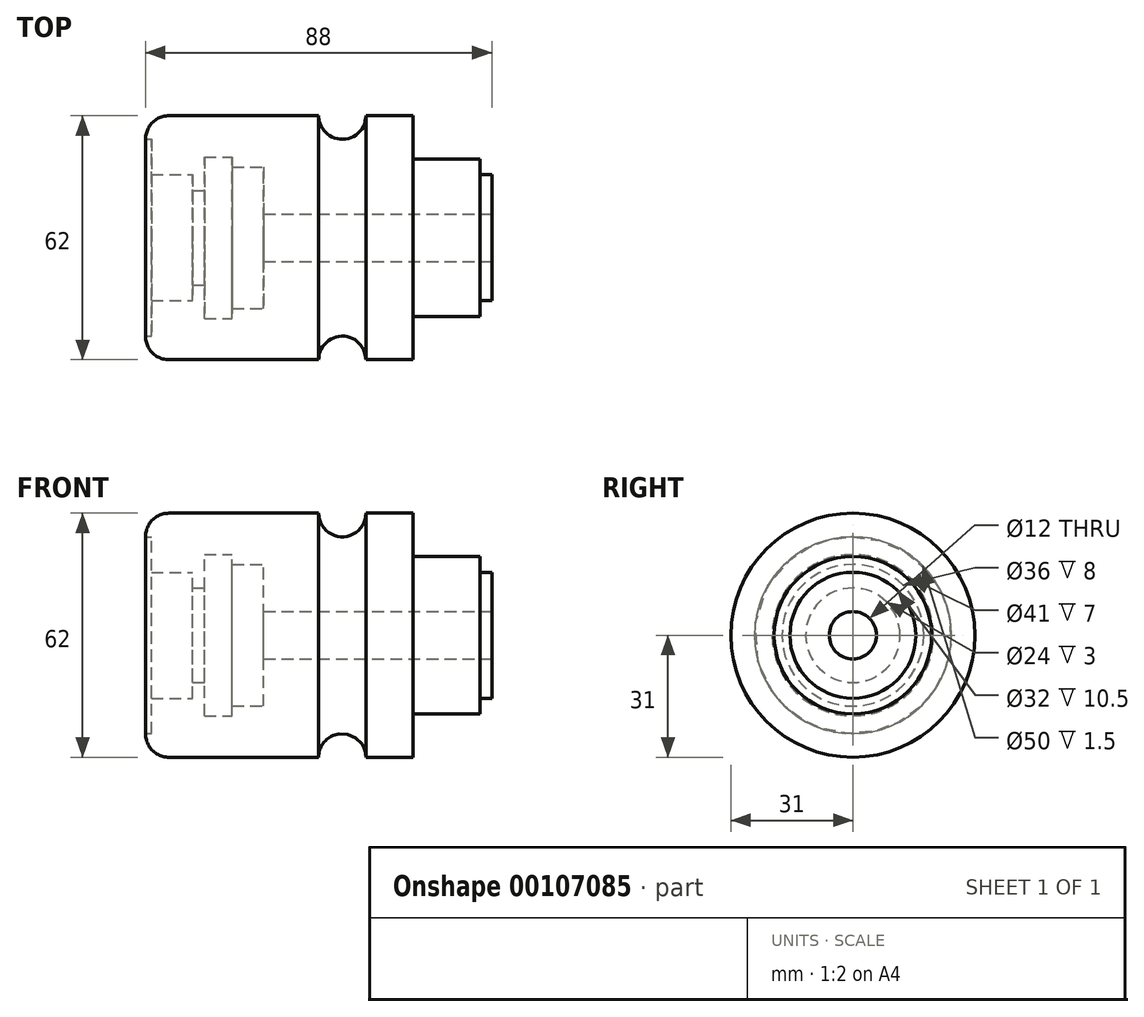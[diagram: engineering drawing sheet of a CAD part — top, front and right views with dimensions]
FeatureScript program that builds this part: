
annotation { "Feature Type Name" : "Feature", "Feature Type Description" : "" }
export const myFeature = defineFeature(function(context is Context, id is Id, definition is map)
    precondition{}
    {
        {
            var Q0;
            Q0=qCreatedBy(makeId("Front.planeOp"),FACE);
            var sketch = newSketch(context, id + "F0", { "sketchPlane" : qUnion([Q0])});
            skLineSegment(sketch, "E0.bottom", {"start": v(0, 0) * mm, "end": v(68, 0) * mm});
            skLineSegment(sketch, "E0.left", {"start": v(0, 0) * mm, "end": v(0, 31) * mm});
            skLineSegment(sketch, "E0.right", {"start": v(68, 0) * mm, "end": v(68, 31) * mm});
            skLineSegment(sketch, "E1.bottom", {"start": v(68, 0) * mm, "end": v(85, 0) * mm});
            skLineSegment(sketch, "E1.top", {"start": v(68, 20) * mm, "end": v(85, 20) * mm});
            skLineSegment(sketch, "E1.left", {"start": v(68, 0) * mm, "end": v(68, 20) * mm});
            skLineSegment(sketch, "E1.right", {"start": v(85, 0) * mm, "end": v(85, 20) * mm});
            skLineSegment(sketch, "E2.bottom", {"start": v(85, 0) * mm, "end": v(88, 0) * mm});
            skLineSegment(sketch, "E2.top", {"start": v(85, 16) * mm, "end": v(88, 16) * mm});
            skLineSegment(sketch, "E2.left", {"start": v(85, 0) * mm, "end": v(85, 16) * mm});
            skLineSegment(sketch, "E2.right", {"start": v(88, 0) * mm, "end": v(88, 16) * mm});
            skLineSegment(sketch, "E3", {"start": v(-75.19, 0) * mm, "end": v(76.5, 0) * mm, "construction": true});
            skArc(sketch, "E4", {"start": v(44, 31) * mm, "mid": v(50, 25) * mm, "end": v(56, 31) * mm});
            skLineSegment(sketch, "E5", {"start": v(0, 31) * mm, "end": v(44, 31) * mm});
            skLineSegment(sketch, "E6", {"start": v(56, 31) * mm, "end": v(68, 31) * mm});
            skSolve(sketch);
        }
        {
            var Q0;
            Q0=makeQuery(id+"F0.imprint","IMPRINT",FACE,{"disambiguationData":[TD([[makeQuery(id+"F0.imprint","IMPRINT",EDGE,{"derivedFrom":sQuery(id+"F0.wireOp",EDGE,"E1.bottom")}),1.0]])]});
            var Q1;
            Q1=makeQuery(id+"F0.imprint","IMPRINT",FACE,{"disambiguationData":[TD([[makeQuery(id+"F0.imprint","IMPRINT",EDGE,{"derivedFrom":sQuery(id+"F0.wireOp",EDGE,"E0.bottom")}),1.0]])]});
            var Q2;
            Q2=makeQuery(id+"F0.imprint","IMPRINT",FACE,{"disambiguationData":[TD([[makeQuery(id+"F0.imprint","IMPRINT",EDGE,{"derivedFrom":sQuery(id+"F0.wireOp",EDGE,"E2.bottom")}),1.0]])]});
            var Q3;
            Q3=sQuery(id+"F0.wireOp",EDGE,"E3");
            revolve(context, id + "F1", {"entities" : qUnion([Q0, Q1, Q2]), "axis" : qUnion([Q3]), "revolveType" : RevolveType.FULL});
        }
        {
            var Q0;
            Q0=qCreatedBy(makeId("Right.planeOp"),FACE);
            var sketch = newSketch(context, id + "F2", { "sketchPlane" : qUnion([Q0])});
            skCircle(sketch, "E7", {"center": v(0, 0) * mm, "radius": 6 * mm});
            skSolve(sketch);
        }
        {
            var Q0;
            Q0 = qSketchRegion(id + "F2", true);
            extrude(context, id + "F3", {"entities" : qUnion([Q0]), "operationType" : NewBodyOperationType.REMOVE, "endBound" : BoundingType.SYMMETRIC, "oppositeDirection" : true, "depth" : 1000 * mm});
        }
        {
            var Q0;
            Q0=qCreatedBy(makeId("Top.planeOp"),FACE);
            var sketch = newSketch(context, id + "F4", { "sketchPlane" : qUnion([Q0])});
            skLineSegment(sketch, "E8.bottom", {"start": v(0, 0) * mm, "end": v(1.5, 0) * mm});
            skLineSegment(sketch, "E8.top", {"start": v(0, 25) * mm, "end": v(1.5, 25) * mm});
            skLineSegment(sketch, "E8.left", {"start": v(0, 0) * mm, "end": v(0, 25) * mm});
            skLineSegment(sketch, "E8.right", {"start": v(1.5, 0) * mm, "end": v(1.5, 25) * mm});
            skLineSegment(sketch, "E9.bottom", {"start": v(0, 0) * mm, "end": v(12, 0) * mm});
            skLineSegment(sketch, "E9.top", {"start": v(0, 16) * mm, "end": v(12, 16) * mm});
            skLineSegment(sketch, "E9.left", {"start": v(0, 0) * mm, "end": v(0, 16) * mm});
            skLineSegment(sketch, "E9.right", {"start": v(12, 0) * mm, "end": v(12, 16) * mm});
            skLineSegment(sketch, "E10.bottom", {"start": v(12, 0) * mm, "end": v(15, 0) * mm});
            skLineSegment(sketch, "E10.top", {"start": v(12, 12) * mm, "end": v(15, 12) * mm});
            skLineSegment(sketch, "E10.left", {"start": v(12, 0) * mm, "end": v(12, 12) * mm});
            skLineSegment(sketch, "E10.right", {"start": v(15, 0) * mm, "end": v(15, 12) * mm});
            skLineSegment(sketch, "E11.left", {"start": v(0, 0) * mm, "end": v(0, 19.39) * mm});
            skLineSegment(sketch, "E12.bottom", {"start": v(15, 0) * mm, "end": v(22, 0) * mm});
            skLineSegment(sketch, "E12.top", {"start": v(15, 20.5) * mm, "end": v(22, 20.5) * mm});
            skLineSegment(sketch, "E12.left", {"start": v(15, 0) * mm, "end": v(15, 20.5) * mm});
            skLineSegment(sketch, "E12.right", {"start": v(22, 0) * mm, "end": v(22, 20.5) * mm});
            skLineSegment(sketch, "E13.bottom", {"start": v(22, 0) * mm, "end": v(30, 0) * mm});
            skLineSegment(sketch, "E13.top", {"start": v(22, 18) * mm, "end": v(30, 18) * mm});
            skLineSegment(sketch, "E13.left", {"start": v(22, 0) * mm, "end": v(22, 18) * mm});
            skLineSegment(sketch, "E13.right", {"start": v(30, 0) * mm, "end": v(30, 18) * mm});
            skLineSegment(sketch, "E14", {"start": v(-74.94, 0) * mm, "end": v(68.1, 0) * mm, "construction": true});
            skSolve(sketch);
        }
        {
            var Q0;
            Q0 = qSketchRegion(id + "F4", true);
            var Q1;
            Q1=sQuery(id+"F4.wireOp",EDGE,"E14");
            revolve(context, id + "F5", {"operationType" : NewBodyOperationType.REMOVE, "entities" : qUnion([Q0]), "axis" : qUnion([Q1]), "revolveType" : RevolveType.FULL, "oppositeDirection" : true});
        }
        {
            var Q0;
            Q0=makeQuery(id+"F1.opRevolve","SWEPT_EDGE",EDGE,{"disambiguationData":[OSD([sQuery(id+"F0.wireOp",EDGE,"E0.left"),sQuery(id+"F0.wireOp",EDGE,"E5")])]});
            fillet(context, id + "F6", {"entities" : qUnion([Q0]), "radius" : 6 * mm, "tangentPropagation" : true, "allowEdgeOverflow" : false});
        }
    });
